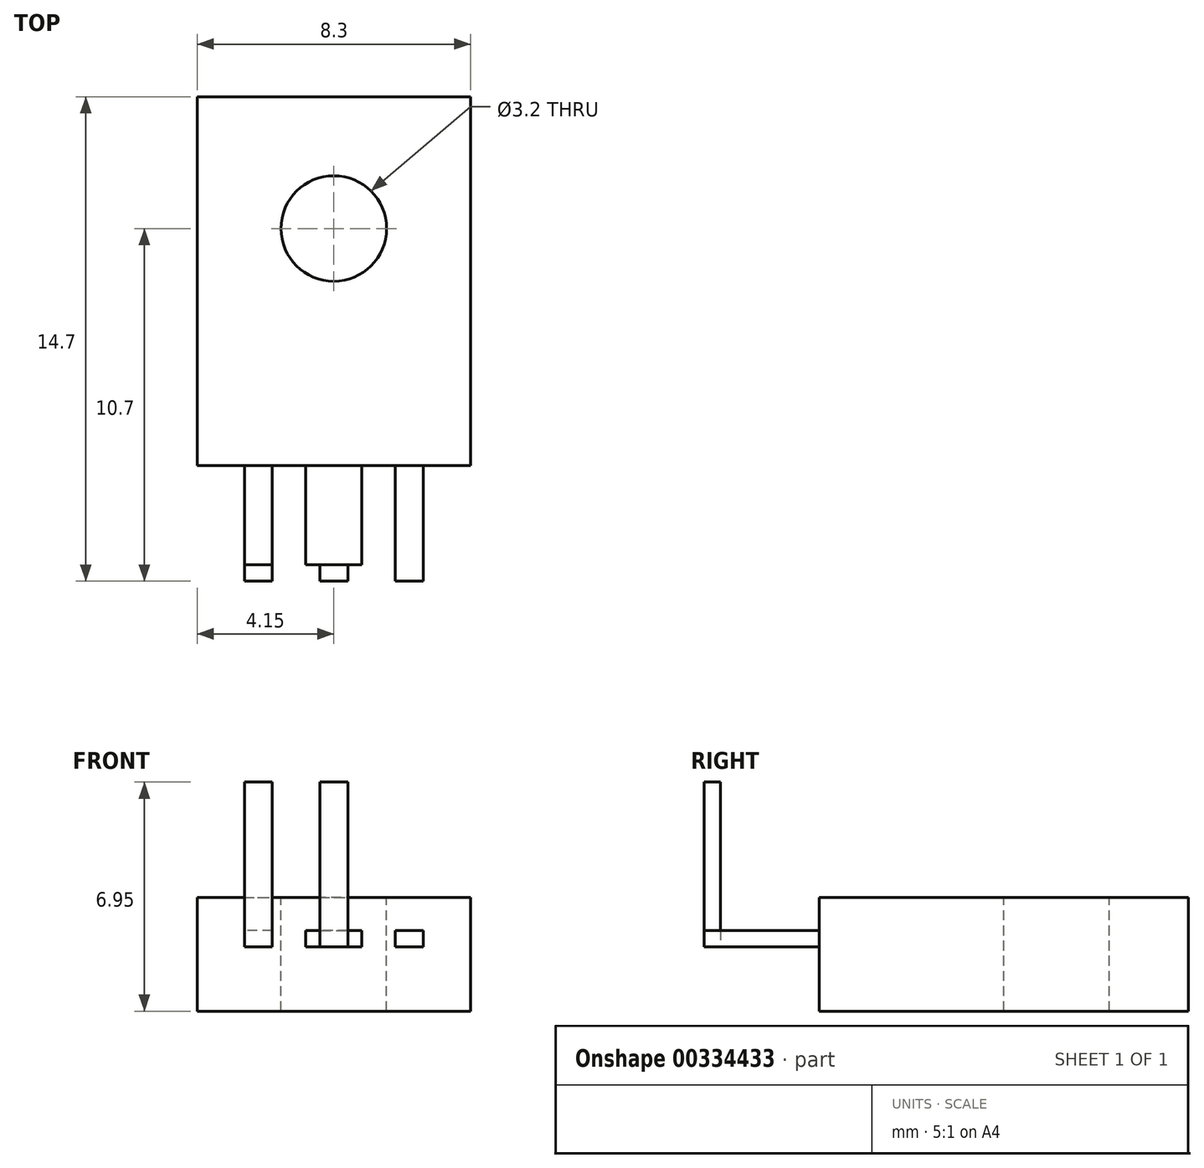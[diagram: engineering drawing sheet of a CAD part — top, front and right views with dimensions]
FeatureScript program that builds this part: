
annotation { "Feature Type Name" : "Feature", "Feature Type Description" : "" }
export const myFeature = defineFeature(function(context is Context, id is Id, definition is map)
    precondition{}
    {
        {
            var Q0;
            Q0=qCreatedBy(makeId("Top.planeOp"),FACE);
            var sketch = newSketch(context, id + "F0", { "sketchPlane" : qUnion([Q0])});
            skLineSegment(sketch, "E0.bottom", {"start": v(-4.15, 5.6) * mm, "end": v(4.15, 5.6) * mm});
            skLineSegment(sketch, "E0.top", {"start": v(-4.15, -5.6) * mm, "end": v(4.15, -5.6) * mm});
            skLineSegment(sketch, "E0.left", {"start": v(-4.15, 5.6) * mm, "end": v(-4.15, -5.6) * mm});
            skLineSegment(sketch, "E0.right", {"start": v(4.15, 5.6) * mm, "end": v(4.15, -5.6) * mm});
            skPoint(sketch, "E0.middle", {"position": v(0, 0) * mm});
            skSolve(sketch);
        }
        {
            var Q0;
            Q0=makeQuery(id+"F0.imprint","IMPRINT",FACE,{"disambiguationData":[TD([[makeQuery(id+"F0.imprint","IMPRINT",EDGE,{"derivedFrom":sQuery(id+"F0.wireOp",EDGE,"E0.bottom")}),-1.0]])]});
            extrude(context, id + "F1", {"entities" : qUnion([Q0]), "depth" : 3.45 * mm});
        }
        {
            var Q0;
            Q0=makeQuery(id+"F1.opExtrude","CAP_FACE",FACE,{"disambiguationData":[OSD([sQuery(id+"F0.wireOp",EDGE,"E0.bottom"),sQuery(id+"F0.wireOp",EDGE,"E0.top"),sQuery(id+"F0.wireOp",EDGE,"E0.left"),sQuery(id+"F0.wireOp",EDGE,"E0.right")])],"isStart":false});
            var sketch = newSketch(context, id + "F2", { "sketchPlane" : qUnion([Q0])});
            skPoint(sketch, "E1", {"position": v(0, 1.6) * mm});
            skPoint(sketch, "E1.positionSnap0", {"position": v(0, 5.6) * mm});
            skSolve(sketch);
        }
        {
            var Q0;
            Q0=sQuery(id+"F2.wireOp",VERTEX,"E1");
            var Q1;
            Q1=makeQuery(id+"F1.opExtrude","SWEPT_BODY",BODY,{"disambiguationData":[OSD([sQuery(id+"F0.wireOp",EDGE,"E0.bottom"),sQuery(id+"F0.wireOp",EDGE,"E0.top"),sQuery(id+"F0.wireOp",EDGE,"E0.left"),sQuery(id+"F0.wireOp",EDGE,"E0.right")])]});
            hole(context, id + "F3", {"style" : HoleStyle.SIMPLE, "endStyle" : HoleEndStyle.THROUGH, "holeDiameter" : 3.2 * mm, "tappedDepth" : 13.2 * mm, "tapClearance" : 3, "startFromSketch" : true, "locations" : qUnion([Q0]), "scope" : qUnion([Q1])});
        }
        {
            var Q0;
            Q0=makeQuery(id+"F1.opExtrude","SWEPT_FACE",FACE,{"disambiguationData":[OSD([sQuery(id+"F0.wireOp",EDGE,"E0.top")])]});
            var sketch = newSketch(context, id + "F4", { "sketchPlane" : qUnion([Q0])});
            skLineSegment(sketch, "E2.bottom", {"start": v(-2.72, 2.45) * mm, "end": v(-1.86, 2.45) * mm});
            skLineSegment(sketch, "E2.top", {"start": v(-2.72, 1.95) * mm, "end": v(-1.86, 1.95) * mm});
            skLineSegment(sketch, "E2.left", {"start": v(-2.71, 2.45) * mm, "end": v(-2.71, 1.95) * mm});
            skLineSegment(sketch, "E2.right", {"start": v(-1.86, 2.45) * mm, "end": v(-1.86, 1.95) * mm});
            skLineSegment(sketch, "E3.bottom", {"start": v(-0.85, 2.45) * mm, "end": v(0.85, 2.45) * mm});
            skLineSegment(sketch, "E3.top", {"start": v(-0.85, 1.95) * mm, "end": v(0.85, 1.95) * mm});
            skLineSegment(sketch, "E3.left", {"start": v(-0.85, 2.45) * mm, "end": v(-0.85, 1.95) * mm});
            skLineSegment(sketch, "E3.right", {"start": v(0.85, 2.45) * mm, "end": v(0.85, 1.95) * mm});
            skLineSegment(sketch, "E4.bottom", {"start": v(1.86, 2.45) * mm, "end": v(2.71, 2.45) * mm});
            skLineSegment(sketch, "E4.top", {"start": v(1.86, 1.95) * mm, "end": v(2.71, 1.95) * mm});
            skLineSegment(sketch, "E4.left", {"start": v(1.87, 2.45) * mm, "end": v(1.87, 1.95) * mm});
            skLineSegment(sketch, "E4.right", {"start": v(2.72, 2.45) * mm, "end": v(2.72, 1.95) * mm});
            skPoint(sketch, "E5", {"position": v(0, 2.45) * mm});
            skPoint(sketch, "E6", {"position": v(-2.3, 2.45) * mm});
            skPoint(sketch, "E7", {"position": v(2.3, 2.45) * mm});
            skSolve(sketch);
        }
        {
            var Q0;
            Q0=makeQuery(id+"F4.imprint","IMPRINT",FACE,{"disambiguationData":[TD([[makeQuery(id+"F4.imprint","IMPRINT",EDGE,{"derivedFrom":sQuery(id+"F4.wireOp",EDGE,"E2.bottom")}),-1.0]])]});
            var Q1;
            Q1=makeQuery(id+"F4.imprint","IMPRINT",FACE,{"disambiguationData":[TD([[makeQuery(id+"F4.imprint","IMPRINT",EDGE,{"derivedFrom":sQuery(id+"F4.wireOp",EDGE,"E3.bottom")}),-1.0]])]});
            var Q2;
            Q2=makeQuery(id+"F4.imprint","IMPRINT",FACE,{"disambiguationData":[TD([[makeQuery(id+"F4.imprint","IMPRINT",EDGE,{"derivedFrom":sQuery(id+"F4.wireOp",EDGE,"E4.bottom")}),-1.0]])]});
            extrude(context, id + "F5", {"entities" : qUnion([Q0, Q1, Q2]), "depth" : 3.5 * mm});
        }
        {
            var Q0;
            Q0=makeQuery(id+"F5.opExtrude","SWEPT_FACE",FACE,{"disambiguationData":[OSD([sQuery(id+"F4.wireOp",EDGE,"E3.top")])]});
            var sketch = newSketch(context, id + "F6", { "sketchPlane" : qUnion([Q0])});
            skLineSegment(sketch, "E8.bottom", {"start": v(-2.71, 9.1) * mm, "end": v(2.72, 9.1) * mm});
            skLineSegment(sketch, "E8.top", {"start": v(-2.71, 8.6) * mm, "end": v(2.72, 8.6) * mm});
            skLineSegment(sketch, "E8.left", {"start": v(-2.71, 9.1) * mm, "end": v(-2.71, 8.6) * mm});
            skLineSegment(sketch, "E8.right", {"start": v(2.72, 9.1) * mm, "end": v(2.72, 8.6) * mm});
            skLineSegment(sketch, "E9", {"start": v(-1.86, 8.6) * mm, "end": v(-1.86, 9.1) * mm});
            skLineSegment(sketch, "E10", {"start": v(-0.42, 9.1) * mm, "end": v(-0.42, 8.6) * mm});
            skLineSegment(sketch, "E11", {"start": v(0.43, 9.1) * mm, "end": v(0.43, 8.6) * mm});
            skLineSegment(sketch, "E12.bottom", {"start": v(1.87, 9.1) * mm, "end": v(2.72, 9.1) * mm});
            skLineSegment(sketch, "E12.top", {"start": v(1.87, 8.6) * mm, "end": v(2.72, 8.6) * mm});
            skLineSegment(sketch, "E12.left", {"start": v(1.87, 9.1) * mm, "end": v(1.87, 8.6) * mm});
            skLineSegment(sketch, "E13", {"start": v(-0.42, 8.85) * mm, "end": v(0.43, 8.85) * mm, "construction": true});
            skPoint(sketch, "E14", {"position": v(0, 8.85) * mm});
            skPoint(sketch, "E15", {"position": v(0, 9.1) * mm});
            skSolve(sketch);
        }
        {
            var Q0;
            Q0=makeQuery(id+"F6.imprint","IMPRINT",FACE,{"disambiguationData":[TD([[makeQuery(id+"F6.imprint","IMPRINT",EDGE,{"derivedFrom":sQuery(id+"F6.wireOp",EDGE,"E12.bottom")}),-1.0]])]});
            var Q1;
            {var subQ0=sQuery(id+"F6.wireOp",EDGE,"E10");Q1=makeQuery(id+"F6.imprint","IMPRINT",FACE,{"disambiguationData":[TD([[makeQuery(id+"F6.imprint","IMPRINT",EDGE,{"derivedFrom":subQ0}),1.0]])]});}
            var Q2;
            {var subQ0=sQuery(id+"F6.wireOp",EDGE,"E8.left");Q2=makeQuery(id+"F6.imprint","IMPRINT",FACE,{"disambiguationData":[TD([[makeQuery(id+"F6.imprint","IMPRINT",EDGE,{"derivedFrom":subQ0}),1.0]])]});}
            extrude(context, id + "F7", {"entities" : qUnion([Q0, Q1, Q2]), "operationType" : NewBodyOperationType.ADD, "oppositeDirection" : true, "depth" : 5 * mm});
        }
        {
            var Q0;
            {var subQ0=sQuery(id+"F6.wireOp",EDGE,"E8.bottom");Q0=makeQuery(id+"F7.boolean.opBoolean","MERGE",FACE,{"derivedFrom":[makeQuery(id+"F5.opExtrude","CAP_FACE",FACE,{"disambiguationData":[OSD([sQuery(id+"F4.wireOp",EDGE,"E3.bottom"),sQuery(id+"F4.wireOp",EDGE,"E3.top"),sQuery(id+"F4.wireOp",EDGE,"E3.left"),sQuery(id+"F4.wireOp",EDGE,"E3.right")])],"isStart":false}),makeQuery(id+"F7.opExtrude","SWEPT_FACE",FACE,{"disambiguationData":[OSD([subQ0]),TDD([makeQuery(id+"F6.imprint","IMPRINT",EDGE,{"disambiguationData":[TD([[makeQuery(id+"F6.imprint","INTERSECT",VERTEX,{"derivedFrom":[subQ0,sQuery(id+"F6.wireOp",EDGE,"E10")]}),-1.0]])],"derivedFrom":subQ0})])]})]});}
            var sketch = newSketch(context, id + "F8", { "sketchPlane" : qUnion([Q0])});
            skLineSegment(sketch, "E16.bottom", {"start": v(-0.85, 2.45) * mm, "end": v(-0.42, 2.45) * mm});
            skLineSegment(sketch, "E16.top", {"start": v(-0.85, 1.95) * mm, "end": v(-0.42, 1.95) * mm});
            skLineSegment(sketch, "E16.left", {"start": v(-0.85, 2.45) * mm, "end": v(-0.85, 1.95) * mm});
            skLineSegment(sketch, "E16.right", {"start": v(-0.42, 2.45) * mm, "end": v(-0.42, 1.95) * mm});
            skLineSegment(sketch, "E17.bottom", {"start": v(0.85, 2.45) * mm, "end": v(0.43, 2.45) * mm});
            skLineSegment(sketch, "E17.top", {"start": v(0.85, 1.95) * mm, "end": v(0.43, 1.95) * mm});
            skLineSegment(sketch, "E17.left", {"start": v(0.85, 2.45) * mm, "end": v(0.85, 1.95) * mm});
            skLineSegment(sketch, "E17.right", {"start": v(0.43, 2.45) * mm, "end": v(0.43, 1.95) * mm});
            skSolve(sketch);
        }
        {
            var Q0;
            Q0=makeQuery(id+"F8.imprint","IMPRINT",FACE,{"disambiguationData":[TD([[makeQuery(id+"F8.imprint","IMPRINT",EDGE,{"derivedFrom":sQuery(id+"F8.wireOp",EDGE,"E16.bottom")}),-1.0]])]});
            var Q1;
            Q1=makeQuery(id+"F8.imprint","IMPRINT",FACE,{"disambiguationData":[TD([[makeQuery(id+"F8.imprint","IMPRINT",EDGE,{"derivedFrom":sQuery(id+"F8.wireOp",EDGE,"E17.bottom")}),-1.0]])]});
            extrude(context, id + "F9", {"entities" : qUnion([Q0, Q1]), "operationType" : NewBodyOperationType.REMOVE, "oppositeDirection" : true, "depth" : 0.5 * mm});
        }
    });
